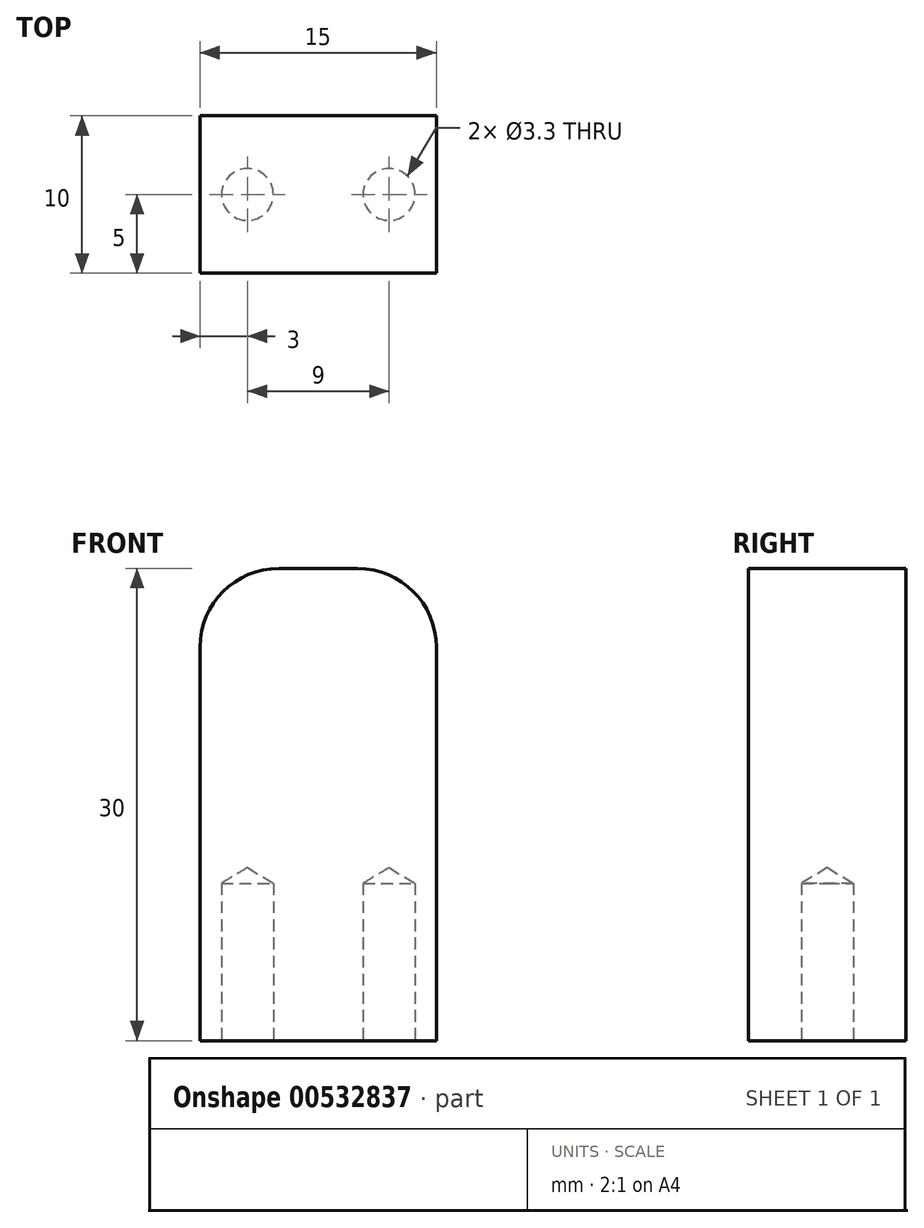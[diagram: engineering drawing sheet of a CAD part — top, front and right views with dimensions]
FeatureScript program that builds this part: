
annotation { "Feature Type Name" : "Feature", "Feature Type Description" : "" }
export const myFeature = defineFeature(function(context is Context, id is Id, definition is map)
    precondition{}
    {
        {
            var Q0;
            Q0=qCreatedBy(makeId("Front.planeOp"),FACE);
            var sketch = newSketch(context, id + "F0", { "sketchPlane" : qUnion([Q0])});
            skLineSegment(sketch, "E0.bottom", {"start": v(-7.5, 30) * mm, "end": v(7.5, 30) * mm});
            skLineSegment(sketch, "E0.top", {"start": v(-7.5, 0) * mm, "end": v(7.5, 0) * mm});
            skLineSegment(sketch, "E0.left", {"start": v(-7.5, 30) * mm, "end": v(-7.5, 0) * mm});
            skLineSegment(sketch, "E0.right", {"start": v(7.5, 30) * mm, "end": v(7.5, 0) * mm});
            skSolve(sketch);
        }
        {
            var Q0;
            Q0 = qSketchRegion(id + "F0", true);
            extrude(context, id + "F1", {"entities" : qUnion([Q0]), "depth" : 10 * mm, "offsetDistance" : 25 * mm});
        }
        {
            var Q0;
            Q0=makeQuery(id+"F1.opExtrude","SWEPT_FACE",FACE,{"disambiguationData":[OSD([sQuery(id+"F0.wireOp",EDGE,"E0.top")])]});
            var sketch = newSketch(context, id + "F2", { "sketchPlane" : qUnion([Q0])});
            skPoint(sketch, "E1", {"position": v(-4.5, 5) * mm});
            skPoint(sketch, "E1.positionSnap0", {"position": v(-7.5, 5) * mm});
            skPoint(sketch, "E2", {"position": v(4.5, 5) * mm});
            skSolve(sketch);
        }
        {
            var Q0;
            Q0=sQuery(id+"F2.wireOp",VERTEX,"E1");
            var Q1;
            Q1=sQuery(id+"F2.wireOp",VERTEX,"E2");
            var Q2;
            Q2=makeQuery(id+"F1.opExtrude","SWEPT_BODY",BODY,{"disambiguationData":[OSD([sQuery(id+"F0.wireOp",EDGE,"E0.bottom"),sQuery(id+"F0.wireOp",EDGE,"E0.top"),sQuery(id+"F0.wireOp",EDGE,"E0.left"),sQuery(id+"F0.wireOp",EDGE,"E0.right")])]});
            hole(context, id + "F3", {"style" : HoleStyle.SIMPLE, "endStyle" : HoleEndStyle.BLIND, "standardTappedOrClearance" : lookupTablePath({ "standard" : "ISO", "engagement" : "75%", "pitch" : "0.7 mm", "size" : "M4", "type" : "Tapped" }), "standardBlindInLast" : lookupTablePath({ "standard" : "ISO", "engagement" : "75%", "pitch" : "0.7 mm", "size" : "M4", "type" : "Tapped" }), "holeDiameter" : 3.3 * mm, "showTappedDepth" : true, "holeDepth" : 10 * mm, "isTappedThrough" : true, "tappedDepth" : 7.9 * mm, "tapClearance" : 3, "startFromSketch" : true, "locations" : qUnion([Q0, Q1]), "scope" : qUnion([Q2]), "majorDiameter" : 4 * mm});
        }
        {
            var Q0;
            Q0=makeQuery(id+"F1.opExtrude","SWEPT_EDGE",EDGE,{"disambiguationData":[OSD([sQuery(id+"F0.wireOp",EDGE,"E0.bottom"),sQuery(id+"F0.wireOp",EDGE,"E0.left")])]});
            var Q1;
            Q1=makeQuery(id+"F1.opExtrude","SWEPT_EDGE",EDGE,{"disambiguationData":[OSD([sQuery(id+"F0.wireOp",EDGE,"E0.bottom"),sQuery(id+"F0.wireOp",EDGE,"E0.right")])]});
            fillet(context, id + "F4", {"entities" : qUnion([Q0, Q1]), "radius" : 5 * mm, "tangentPropagation" : true, "allowEdgeOverflow" : false});
        }
    });
